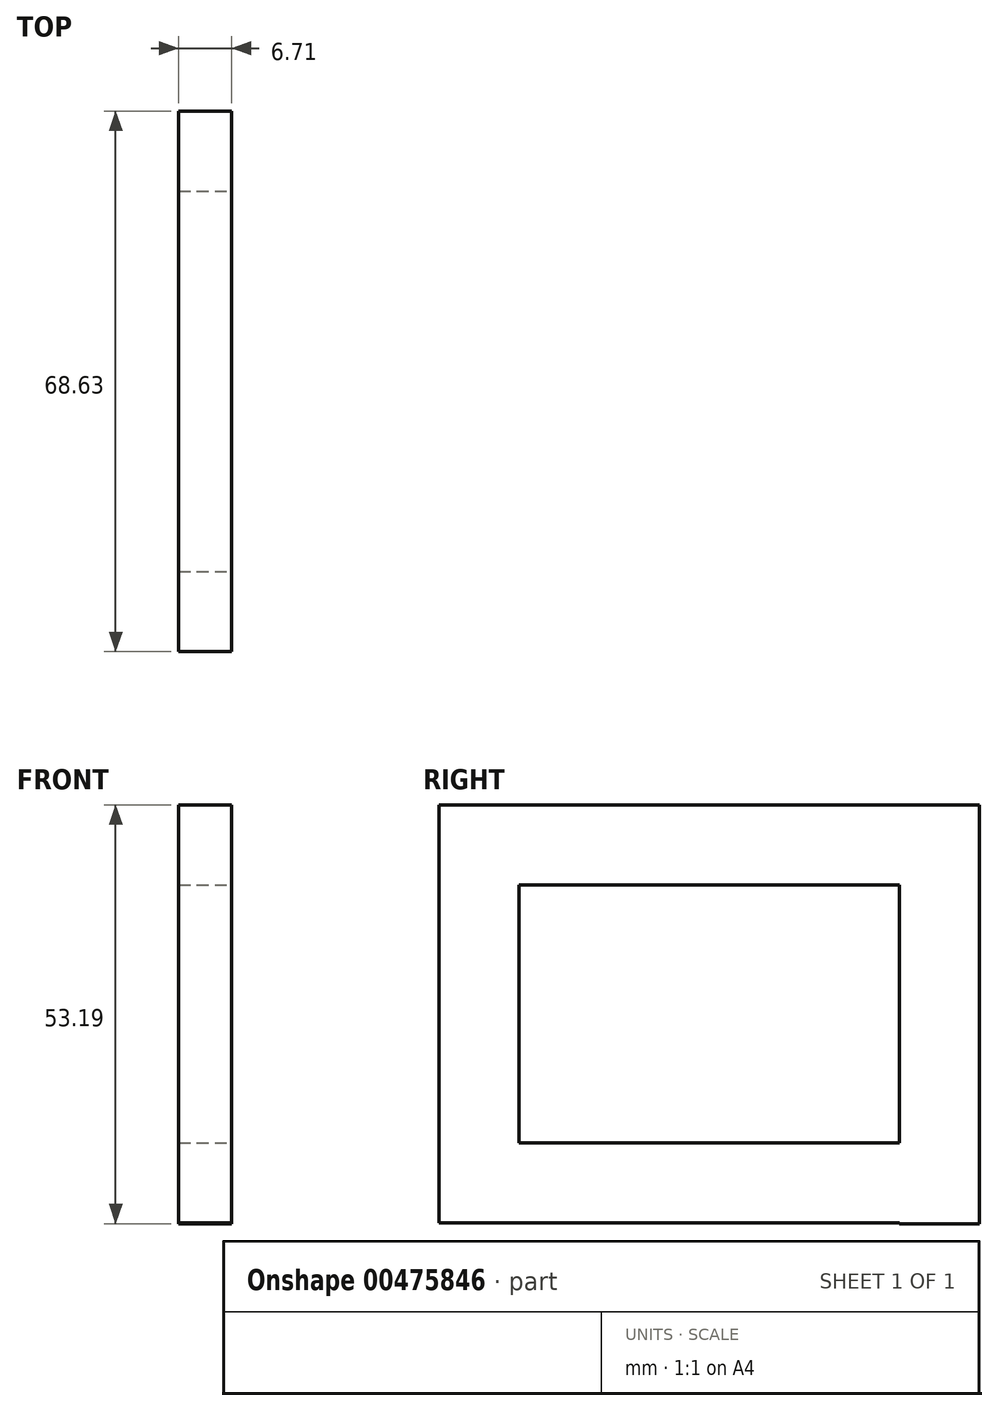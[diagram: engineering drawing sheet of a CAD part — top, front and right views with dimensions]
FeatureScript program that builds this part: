
annotation { "Feature Type Name" : "Feature", "Feature Type Description" : "" }
export const myFeature = defineFeature(function(context is Context, id is Id, definition is map)
    precondition{}
    {
        {
            var Q0;
            Q0=qCreatedBy(makeId("Top.planeOp"),FACE);
            var sketch = newSketch(context, id + "F0", { "sketchPlane" : qUnion([Q0])});
            skLineSegment(sketch, "E0.bottom", {"start": v(0, 0) * mm, "end": v(6.7, 0) * mm});
            skLineSegment(sketch, "E0.top", {"start": v(0, -48.31) * mm, "end": v(6.7, -48.31) * mm});
            skLineSegment(sketch, "E0.left", {"start": v(0, 0) * mm, "end": v(0, -48.31) * mm});
            skLineSegment(sketch, "E0.right", {"start": v(6.7, 0) * mm, "end": v(6.7, -48.31) * mm});
            skSolve(sketch);
        }
        {
            var Q0;
            Q0 = qSketchRegion(id + "F0", true);
            extrude(context, id + "F1", {"entities" : qUnion([Q0]), "depth" : 10.16 * mm});
        }
        {
            var Q0;
            Q0=makeQuery(id+"F1.opExtrude","SWEPT_FACE",FACE,{"disambiguationData":[OSD([sQuery(id+"F0.wireOp",EDGE,"E0.bottom")])]});
            var sketch = newSketch(context, id + "F2", { "sketchPlane" : qUnion([Q0])});
            skPoint(sketch, "E1.oppositeSnap0", {"position": v(0, 5.08) * mm});
            skLineSegment(sketch, "E1.bottom", {"start": v(-6.7, 10.16) * mm, "end": v(0, 10.16) * mm});
            skLineSegment(sketch, "E1.top", {"start": v(-6.7, -32.87) * mm, "end": v(0, -32.87) * mm});
            skLineSegment(sketch, "E1.left", {"start": v(-6.7, 10.16) * mm, "end": v(-6.7, -32.87) * mm});
            skLineSegment(sketch, "E1.right", {"start": v(0, 10.16) * mm, "end": v(0, -32.87) * mm});
            skSolve(sketch);
        }
        {
            var Q0;
            Q0 = qSketchRegion(id + "F2", true);
            extrude(context, id + "F3", {"entities" : qUnion([Q0]), "operationType" : NewBodyOperationType.ADD, "depth" : 10.16 * mm});
        }
        {
            var Q0;
            Q0=makeQuery(id+"F1.opExtrude","SWEPT_FACE",FACE,{"disambiguationData":[OSD([sQuery(id+"F0.wireOp",EDGE,"E0.top")])]});
            var sketch = newSketch(context, id + "F4", { "sketchPlane" : qUnion([Q0])});
            skLineSegment(sketch, "E2.bottom", {"start": v(6.7, 10.16) * mm, "end": v(0, 10.16) * mm});
            skLineSegment(sketch, "E2.top", {"start": v(6.7, -32.77) * mm, "end": v(0, -32.77) * mm});
            skLineSegment(sketch, "E2.left", {"start": v(6.7, 10.16) * mm, "end": v(6.7, -32.77) * mm});
            skLineSegment(sketch, "E2.right", {"start": v(0, 10.16) * mm, "end": v(0, -32.77) * mm});
            skSolve(sketch);
        }
        {
            var Q0;
            Q0 = qSketchRegion(id + "F4", true);
            extrude(context, id + "F5", {"entities" : qUnion([Q0]), "operationType" : NewBodyOperationType.ADD, "depth" : 10.16 * mm});
        }
        {
            var Q0;
            Q0=makeQuery(id+"F5.opExtrude","SWEPT_FACE",FACE,{"disambiguationData":[OSD([sQuery(id+"F4.wireOp",EDGE,"E2.top")])]});
            var sketch = newSketch(context, id + "F6", { "sketchPlane" : qUnion([Q0])});
            skLineSegment(sketch, "E3.bottom", {"start": v(0, 58.47) * mm, "end": v(6.7, 58.47) * mm});
            skLineSegment(sketch, "E3.top", {"start": v(0, 0) * mm, "end": v(6.7, 0) * mm});
            skLineSegment(sketch, "E3.left", {"start": v(0, 58.47) * mm, "end": v(0, 0) * mm});
            skLineSegment(sketch, "E3.right", {"start": v(6.7, 58.47) * mm, "end": v(6.7, 0) * mm});
            skSolve(sketch);
        }
        {
            var Q0;
            Q0 = qSketchRegion(id + "F6", true);
            extrude(context, id + "F7", {"entities" : qUnion([Q0]), "operationType" : NewBodyOperationType.ADD, "depth" : 10.16 * mm});
        }
        {
            var Q0;
            Q0=makeQuery(id+"F3.opExtrude","SWEPT_FACE",FACE,{"disambiguationData":[OSD([sQuery(id+"F2.wireOp",EDGE,"E1.top")])]});
            var sketch = newSketch(context, id + "F8", { "sketchPlane" : qUnion([Q0])});
            skLineSegment(sketch, "E4.bottom", {"start": v(0, -10.16) * mm, "end": v(6.7, -10.16) * mm});
            skLineSegment(sketch, "E4.top", {"start": v(0, 0) * mm, "end": v(6.7, 0) * mm});
            skLineSegment(sketch, "E4.left", {"start": v(0, -10.16) * mm, "end": v(0, 0) * mm});
            skLineSegment(sketch, "E4.right", {"start": v(6.7, -10.16) * mm, "end": v(6.7, 0) * mm});
            skSolve(sketch);
        }
        {
            var Q0;
            Q0 = qSketchRegion(id + "F8", true);
            extrude(context, id + "F9", {"entities" : qUnion([Q0]), "operationType" : NewBodyOperationType.ADD, "depth" : 10.16 * mm});
        }
    });
